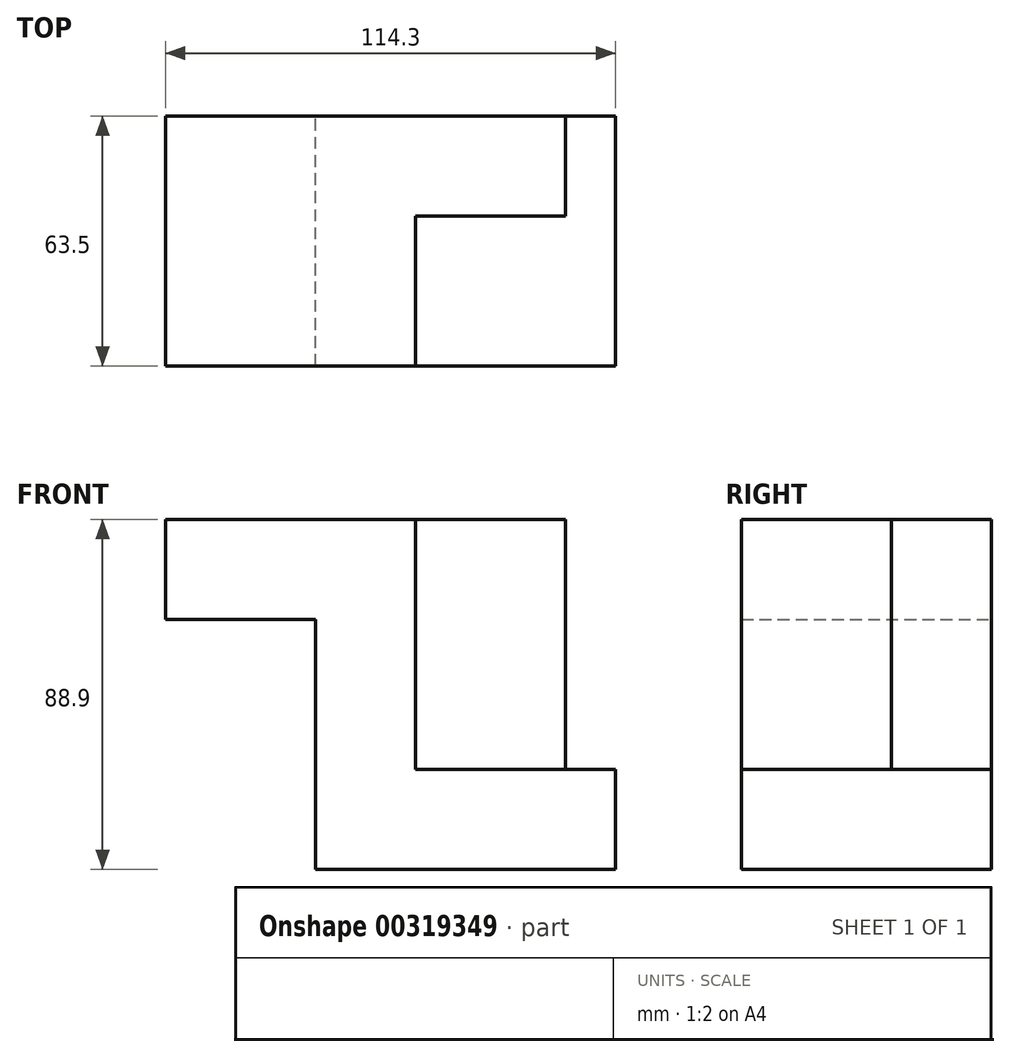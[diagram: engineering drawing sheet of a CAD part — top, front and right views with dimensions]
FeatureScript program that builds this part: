
annotation { "Feature Type Name" : "Feature", "Feature Type Description" : "" }
export const myFeature = defineFeature(function(context is Context, id is Id, definition is map)
    precondition{}
    {
        {
            var Q0;
            Q0=qCreatedBy(makeId("Front.planeOp"),FACE);
            var sketch = newSketch(context, id + "F0", { "sketchPlane" : qUnion([Q0])});
            skLineSegment(sketch, "E0", {"start": v(-84.05, 64.34) * mm, "end": v(-20.55, 64.34) * mm});
            skLineSegment(sketch, "E1", {"start": v(-20.55, 64.34) * mm, "end": v(-20.55, 0.84) * mm});
            skLineSegment(sketch, "E2", {"start": v(-20.55, 0.84) * mm, "end": v(30.25, 0.84) * mm});
            skLineSegment(sketch, "E3", {"start": v(30.25, 0.84) * mm, "end": v(30.25, -24.56) * mm});
            skLineSegment(sketch, "E4", {"start": v(30.25, -24.56) * mm, "end": v(-45.95, -24.56) * mm});
            skLineSegment(sketch, "E5", {"start": v(-45.95, -24.56) * mm, "end": v(-45.95, 38.94) * mm});
            skLineSegment(sketch, "E6", {"start": v(-45.95, 38.94) * mm, "end": v(-84.05, 38.94) * mm});
            skLineSegment(sketch, "E7", {"start": v(-84.05, 38.94) * mm, "end": v(-84.05, 64.34) * mm});
            skSolve(sketch);
        }
        {
            var Q0;
            Q0=makeQuery(id+"F0.imprint","IMPRINT",FACE,{"disambiguationData":[TD([[makeQuery(id+"F0.imprint","IMPRINT",EDGE,{"derivedFrom":sQuery(id+"F0.wireOp",EDGE,"E0")}),-1.0]])]});
            extrude(context, id + "F1", {"entities" : qUnion([Q0]), "depth" : 63.5 * mm});
        }
        {
            var Q0;
            Q0=makeQuery(id+"F1.opExtrude","SWEPT_FACE",FACE,{"disambiguationData":[OSD([sQuery(id+"F0.wireOp",EDGE,"E1")])]});
            var sketch = newSketch(context, id + "F2", { "sketchPlane" : qUnion([Q0])});
            skLineSegment(sketch, "E8.bottom", {"start": v(-25.4, 64.34) * mm, "end": v(0, 64.34) * mm});
            skLineSegment(sketch, "E8.top", {"start": v(-25.4, 0.84) * mm, "end": v(0, 0.84) * mm});
            skLineSegment(sketch, "E8.left", {"start": v(-25.4, 64.34) * mm, "end": v(-25.4, 0.84) * mm});
            skLineSegment(sketch, "E8.right", {"start": v(0, 64.34) * mm, "end": v(0, 0.84) * mm});
            skSolve(sketch);
        }
        {
            var Q0;
            Q0=makeQuery(id+"F2.imprint","IMPRINT",FACE,{"disambiguationData":[TD([[makeQuery(id+"F2.imprint","IMPRINT",EDGE,{"derivedFrom":sQuery(id+"F2.wireOp",EDGE,"E8.bottom")}),-1.0]])]});
            extrude(context, id + "F3", {"entities" : qUnion([Q0]), "operationType" : NewBodyOperationType.ADD, "depth" : 38.1 * mm});
        }
    });
